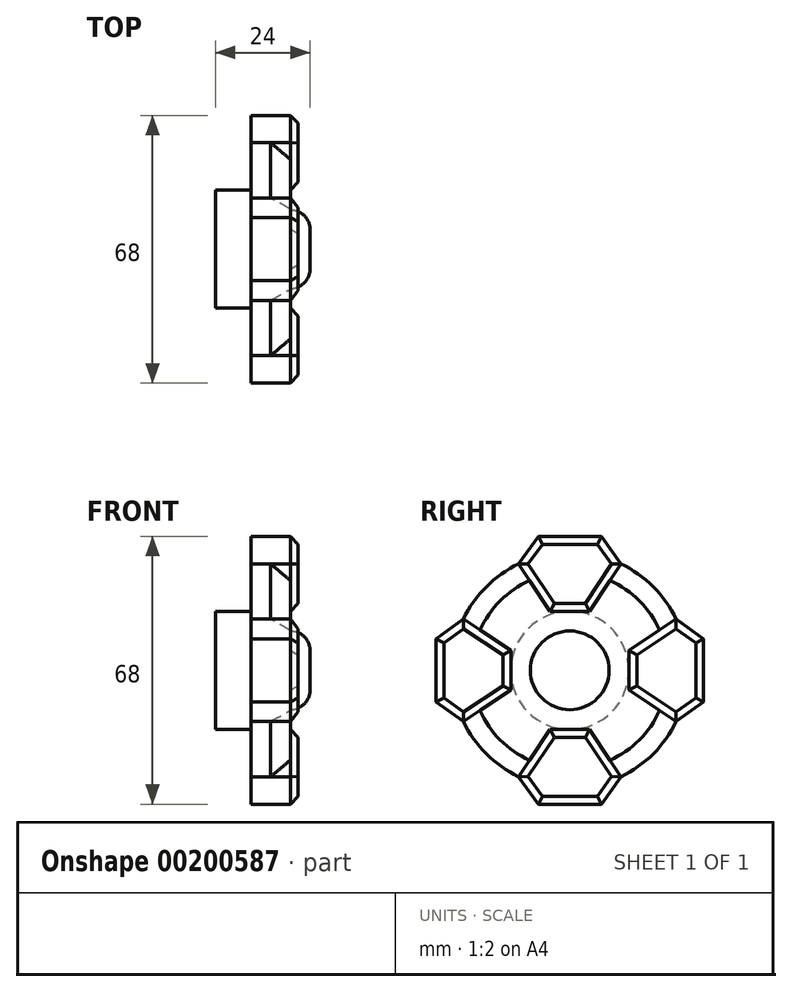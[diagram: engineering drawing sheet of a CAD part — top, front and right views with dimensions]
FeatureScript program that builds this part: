
annotation { "Feature Type Name" : "Feature", "Feature Type Description" : "" }
export const myFeature = defineFeature(function(context is Context, id is Id, definition is map)
    precondition{}
    {
        {
            var Q0;
            Q0=qCreatedBy(makeId("Right.planeOp"),FACE);
            var sketch = newSketch(context, id + "F0", { "sketchPlane" : qUnion([Q0])});
            skCircle(sketch, "E0", {"center": v(0, 0) * mm, "radius": 30 * mm});
            skLineSegment(sketch, "E1", {"start": v(0, 0) * mm, "end": v(0, 30) * mm, "construction": true});
            skLineSegment(sketch, "E2", {"start": v(0, 34) * mm, "end": v(-8, 34) * mm});
            skLineSegment(sketch, "E3", {"start": v(-8, 34) * mm, "end": v(-13, 27.04) * mm});
            skLineSegment(sketch, "E4", {"start": v(-13, 27.04) * mm, "end": v(-5, 15) * mm});
            skLineSegment(sketch, "E5", {"start": v(-5, 15) * mm, "end": v(0, 15) * mm});
            skLineSegment(sketch, "E6.MirrorCS", {"start": v(0, 34) * mm, "end": v(8, 34) * mm});
            skLineSegment(sketch, "E7.MirrorCS", {"start": v(8, 34) * mm, "end": v(13, 27.04) * mm});
            skLineSegment(sketch, "E8.MirrorCS", {"start": v(13, 27.04) * mm, "end": v(5, 15) * mm});
            skLineSegment(sketch, "E9.MirrorCS", {"start": v(5, 15) * mm, "end": v(0, 15) * mm});
            skLineSegment(sketch, "E10.1.0", {"start": v(-34, 8) * mm, "end": v(-27.04, 13) * mm});
            skLineSegment(sketch, "E10.1.1", {"start": v(-34, 0) * mm, "end": v(-34, 8) * mm});
            skLineSegment(sketch, "E10.1.2", {"start": v(-34, 0) * mm, "end": v(-34, -8) * mm});
            skLineSegment(sketch, "E10.1.3", {"start": v(-34, -8) * mm, "end": v(-27.04, -13) * mm});
            skLineSegment(sketch, "E10.1.4", {"start": v(-27.04, -13) * mm, "end": v(-15, -5) * mm});
            skLineSegment(sketch, "E10.1.5", {"start": v(-27.04, 13) * mm, "end": v(-15, 5) * mm});
            skLineSegment(sketch, "E10.1.6", {"start": v(-15, 5) * mm, "end": v(-15, 0) * mm});
            skLineSegment(sketch, "E10.1.7", {"start": v(-15, -5) * mm, "end": v(-15, 0) * mm});
            skLineSegment(sketch, "E10.2.0", {"start": v(-8, -34) * mm, "end": v(-13, -27.04) * mm});
            skLineSegment(sketch, "E10.2.1", {"start": v(0, -34) * mm, "end": v(-8, -34) * mm});
            skLineSegment(sketch, "E10.2.2", {"start": v(0, -34) * mm, "end": v(8, -34) * mm});
            skLineSegment(sketch, "E10.2.3", {"start": v(8, -34) * mm, "end": v(13, -27.04) * mm});
            skLineSegment(sketch, "E10.2.4", {"start": v(13, -27.04) * mm, "end": v(5, -15) * mm});
            skLineSegment(sketch, "E10.2.5", {"start": v(-13, -27.04) * mm, "end": v(-5, -15) * mm});
            skLineSegment(sketch, "E10.2.6", {"start": v(-5, -15) * mm, "end": v(0, -15) * mm});
            skLineSegment(sketch, "E10.2.7", {"start": v(5, -15) * mm, "end": v(0, -15) * mm});
            skLineSegment(sketch, "E10.3.0", {"start": v(34, -8) * mm, "end": v(27.04, -13) * mm});
            skLineSegment(sketch, "E10.3.1", {"start": v(34, 0) * mm, "end": v(34, -8) * mm});
            skLineSegment(sketch, "E10.3.2", {"start": v(34, 0) * mm, "end": v(34, 8) * mm});
            skLineSegment(sketch, "E10.3.3", {"start": v(34, 8) * mm, "end": v(27.04, 13) * mm});
            skLineSegment(sketch, "E10.3.4", {"start": v(27.04, 13) * mm, "end": v(15, 5) * mm});
            skLineSegment(sketch, "E10.3.5", {"start": v(27.04, -13) * mm, "end": v(15, -5) * mm});
            skLineSegment(sketch, "E10.3.6", {"start": v(15, -5) * mm, "end": v(15, 0) * mm});
            skLineSegment(sketch, "E10.3.7", {"start": v(15, 5) * mm, "end": v(15, 0) * mm});
            skSolve(sketch);
        }
        {
            var Q0;
            {var subQ2=sQuery(id+"F0.wireOp",EDGE,"E4");Q0=makeQuery(id+"F0.imprint","IMPRINT",FACE,{"disambiguationData":[TD([[makeQuery(id+"F0.imprint","IMPRINT",EDGE,{"derivedFrom":subQ2}),-1.0]])]});}
            extrude(context, id + "F1", {"entities" : qUnion([Q0]), "depth" : 10 * mm});
        }
        {
            var Q0;
            {var subQ1=sQuery(id+"F0.wireOp",EDGE,"E10.3.4");Q0=makeQuery(id+"F0.imprint","IMPRINT",FACE,{"disambiguationData":[TD([[makeQuery(id+"F0.imprint","IMPRINT",EDGE,{"derivedFrom":subQ1}),1.0]])]});}
            var Q1;
            {var subQ0=sQuery(id+"F0.wireOp",EDGE,"E10.3.0");Q1=makeQuery(id+"F0.imprint","IMPRINT",FACE,{"disambiguationData":[TD([[makeQuery(id+"F0.imprint","IMPRINT",EDGE,{"derivedFrom":subQ0}),-1.0]])]});}
            var Q2;
            {var subQ1=sQuery(id+"F0.wireOp",EDGE,"E4");Q2=makeQuery(id+"F0.imprint","IMPRINT",FACE,{"disambiguationData":[TD([[makeQuery(id+"F0.imprint","IMPRINT",EDGE,{"derivedFrom":subQ1}),1.0]])]});}
            var Q3;
            Q3=makeQuery(id+"F0.imprint","IMPRINT",FACE,{"disambiguationData":[TD([[makeQuery(id+"F0.imprint","IMPRINT",EDGE,{"derivedFrom":sQuery(id+"F0.wireOp",EDGE,"E2")}),1.0]])]});
            var Q4;
            {var subQ1=sQuery(id+"F0.wireOp",EDGE,"E10.1.4");Q4=makeQuery(id+"F0.imprint","IMPRINT",FACE,{"disambiguationData":[TD([[makeQuery(id+"F0.imprint","IMPRINT",EDGE,{"derivedFrom":subQ1}),1.0]])]});}
            var Q5;
            {var subQ0=sQuery(id+"F0.wireOp",EDGE,"E10.1.0");Q5=makeQuery(id+"F0.imprint","IMPRINT",FACE,{"disambiguationData":[TD([[makeQuery(id+"F0.imprint","IMPRINT",EDGE,{"derivedFrom":subQ0}),-1.0]])]});}
            var Q6;
            {var subQ1=sQuery(id+"F0.wireOp",EDGE,"E10.2.4");Q6=makeQuery(id+"F0.imprint","IMPRINT",FACE,{"disambiguationData":[TD([[makeQuery(id+"F0.imprint","IMPRINT",EDGE,{"derivedFrom":subQ1}),1.0]])]});}
            var Q7;
            {var subQ0=sQuery(id+"F0.wireOp",EDGE,"E10.2.0");Q7=makeQuery(id+"F0.imprint","IMPRINT",FACE,{"disambiguationData":[TD([[makeQuery(id+"F0.imprint","IMPRINT",EDGE,{"derivedFrom":subQ0}),-1.0]])]});}
            extrude(context, id + "F2", {"entities" : qUnion([Q0, Q1, Q2, Q3, Q4, Q5, Q6, Q7]), "operationType" : NewBodyOperationType.ADD, "depth" : 12 * mm});
        }
        {
            var Q0;
            {var subQ0=sQuery(id+"F0.wireOp",EDGE,"E0");Q0=makeQuery(id+"F1.opExtrude","CAP_EDGE",EDGE,{"disambiguationData":[OSD([subQ0]),TDD([makeQuery(id+"F0.imprint","IMPRINT",EDGE,{"disambiguationData":[TD([[makeQuery(id+"F0.imprint","INTERSECT",VERTEX,{"derivedFrom":[subQ0,sQuery(id+"F0.wireOp",EDGE,"E7.MirrorCS"),sQuery(id+"F0.wireOp",EDGE,"E8.MirrorCS")]}),1.0]])],"derivedFrom":subQ0})])],"isStart":false});}
            var Q1;
            {var subQ0=sQuery(id+"F0.wireOp",EDGE,"E0");Q1=makeQuery(id+"F1.opExtrude","CAP_EDGE",EDGE,{"disambiguationData":[OSD([subQ0]),TDD([makeQuery(id+"F0.imprint","IMPRINT",EDGE,{"disambiguationData":[TD([[makeQuery(id+"F0.imprint","INTERSECT",VERTEX,{"derivedFrom":[subQ0,sQuery(id+"F0.wireOp",EDGE,"E3"),sQuery(id+"F0.wireOp",EDGE,"E4")]}),-1.0]])],"derivedFrom":subQ0})])],"isStart":false});}
            var Q2;
            {var subQ0=sQuery(id+"F0.wireOp",EDGE,"E0");Q2=makeQuery(id+"F1.opExtrude","CAP_EDGE",EDGE,{"disambiguationData":[OSD([subQ0]),TDD([makeQuery(id+"F0.imprint","IMPRINT",EDGE,{"disambiguationData":[TD([[makeQuery(id+"F0.imprint","INTERSECT",VERTEX,{"derivedFrom":[subQ0,sQuery(id+"F0.wireOp",EDGE,"E10.1.3"),sQuery(id+"F0.wireOp",EDGE,"E10.1.4")]}),-1.0]])],"derivedFrom":subQ0})])],"isStart":false});}
            var Q3;
            {var subQ0=sQuery(id+"F0.wireOp",EDGE,"E0");Q3=makeQuery(id+"F1.opExtrude","CAP_EDGE",EDGE,{"disambiguationData":[OSD([subQ0]),TDD([makeQuery(id+"F0.imprint","IMPRINT",EDGE,{"disambiguationData":[TD([[makeQuery(id+"F0.imprint","INTERSECT",VERTEX,{"derivedFrom":[subQ0,sQuery(id+"F0.wireOp",EDGE,"E10.2.3"),sQuery(id+"F0.wireOp",EDGE,"E10.2.4")]}),-1.0]])],"derivedFrom":subQ0})])],"isStart":false});}
            chamfer(context, id + "F3", {"entities" : qUnion([Q0, Q1, Q2, Q3]), "width" : 5 * mm, "tangentPropagation" : true});
        }
        {
            var Q0;
            Q0=makeQuery(id+"F2.opExtrude","CAP_EDGE",EDGE,{"disambiguationData":[OSD([sQuery(id+"F0.wireOp",EDGE,"E2"),sQuery(id+"F0.wireOp",EDGE,"E6.MirrorCS")])],"isStart":false});
            var Q1;
            Q1=makeQuery(id+"F2.opExtrude","CAP_EDGE",EDGE,{"disambiguationData":[OSD([sQuery(id+"F0.wireOp",EDGE,"E3")])],"isStart":false});
            var Q2;
            Q2=makeQuery(id+"F2.opExtrude","CAP_EDGE",EDGE,{"disambiguationData":[OSD([sQuery(id+"F0.wireOp",EDGE,"E7.MirrorCS")])],"isStart":false});
            var Q3;
            Q3=makeQuery(id+"F2.opExtrude","CAP_EDGE",EDGE,{"disambiguationData":[OSD([sQuery(id+"F0.wireOp",EDGE,"E4")])],"isStart":false});
            var Q4;
            Q4=makeQuery(id+"F2.opExtrude","CAP_EDGE",EDGE,{"disambiguationData":[OSD([sQuery(id+"F0.wireOp",EDGE,"E8.MirrorCS")])],"isStart":false});
            var Q5;
            Q5=makeQuery(id+"F2.opExtrude","CAP_EDGE",EDGE,{"disambiguationData":[OSD([sQuery(id+"F0.wireOp",EDGE,"E5"),sQuery(id+"F0.wireOp",EDGE,"E9.MirrorCS")])],"isStart":false});
            var Q6;
            Q6=makeQuery(id+"F2.opExtrude","CAP_EDGE",EDGE,{"disambiguationData":[OSD([sQuery(id+"F0.wireOp",EDGE,"E10.1.6"),sQuery(id+"F0.wireOp",EDGE,"E10.1.7")])],"isStart":false});
            var Q7;
            Q7=makeQuery(id+"F2.opExtrude","CAP_EDGE",EDGE,{"disambiguationData":[OSD([sQuery(id+"F0.wireOp",EDGE,"E10.1.5")])],"isStart":false});
            var Q8;
            Q8=makeQuery(id+"F2.opExtrude","CAP_EDGE",EDGE,{"disambiguationData":[OSD([sQuery(id+"F0.wireOp",EDGE,"E10.1.0")])],"isStart":false});
            var Q9;
            Q9=makeQuery(id+"F2.opExtrude","CAP_EDGE",EDGE,{"disambiguationData":[OSD([sQuery(id+"F0.wireOp",EDGE,"E10.1.1"),sQuery(id+"F0.wireOp",EDGE,"E10.1.2")])],"isStart":false});
            var Q10;
            Q10=makeQuery(id+"F2.opExtrude","CAP_EDGE",EDGE,{"disambiguationData":[OSD([sQuery(id+"F0.wireOp",EDGE,"E10.1.3")])],"isStart":false});
            var Q11;
            Q11=makeQuery(id+"F2.opExtrude","CAP_EDGE",EDGE,{"disambiguationData":[OSD([sQuery(id+"F0.wireOp",EDGE,"E10.1.4")])],"isStart":false});
            var Q12;
            Q12=makeQuery(id+"F2.opExtrude","CAP_EDGE",EDGE,{"disambiguationData":[OSD([sQuery(id+"F0.wireOp",EDGE,"E10.2.6"),sQuery(id+"F0.wireOp",EDGE,"E10.2.7")])],"isStart":false});
            var Q13;
            Q13=makeQuery(id+"F2.opExtrude","CAP_EDGE",EDGE,{"disambiguationData":[OSD([sQuery(id+"F0.wireOp",EDGE,"E10.2.5")])],"isStart":false});
            var Q14;
            Q14=makeQuery(id+"F2.opExtrude","CAP_EDGE",EDGE,{"disambiguationData":[OSD([sQuery(id+"F0.wireOp",EDGE,"E10.2.0")])],"isStart":false});
            var Q15;
            Q15=makeQuery(id+"F2.opExtrude","CAP_EDGE",EDGE,{"disambiguationData":[OSD([sQuery(id+"F0.wireOp",EDGE,"E10.2.1"),sQuery(id+"F0.wireOp",EDGE,"E10.2.2")])],"isStart":false});
            var Q16;
            Q16=makeQuery(id+"F2.opExtrude","CAP_EDGE",EDGE,{"disambiguationData":[OSD([sQuery(id+"F0.wireOp",EDGE,"E10.2.3")])],"isStart":false});
            var Q17;
            Q17=makeQuery(id+"F2.opExtrude","CAP_EDGE",EDGE,{"disambiguationData":[OSD([sQuery(id+"F0.wireOp",EDGE,"E10.2.4")])],"isStart":false});
            var Q18;
            Q18=makeQuery(id+"F2.opExtrude","CAP_EDGE",EDGE,{"disambiguationData":[OSD([sQuery(id+"F0.wireOp",EDGE,"E10.3.6"),sQuery(id+"F0.wireOp",EDGE,"E10.3.7")])],"isStart":false});
            var Q19;
            Q19=makeQuery(id+"F2.opExtrude","CAP_EDGE",EDGE,{"disambiguationData":[OSD([sQuery(id+"F0.wireOp",EDGE,"E10.3.4")])],"isStart":false});
            var Q20;
            Q20=makeQuery(id+"F2.opExtrude","CAP_EDGE",EDGE,{"disambiguationData":[OSD([sQuery(id+"F0.wireOp",EDGE,"E10.3.3")])],"isStart":false});
            var Q21;
            Q21=makeQuery(id+"F2.opExtrude","CAP_EDGE",EDGE,{"disambiguationData":[OSD([sQuery(id+"F0.wireOp",EDGE,"E10.3.1"),sQuery(id+"F0.wireOp",EDGE,"E10.3.2")])],"isStart":false});
            var Q22;
            Q22=makeQuery(id+"F2.opExtrude","CAP_EDGE",EDGE,{"disambiguationData":[OSD([sQuery(id+"F0.wireOp",EDGE,"E10.3.5")])],"isStart":false});
            var Q23;
            Q23=makeQuery(id+"F2.opExtrude","CAP_EDGE",EDGE,{"disambiguationData":[OSD([sQuery(id+"F0.wireOp",EDGE,"E10.3.0")])],"isStart":false});
            chamfer(context, id + "F4", {"entities" : qUnion([Q0, Q1, Q2, Q3, Q4, Q5, Q6, Q7, Q8, Q9, Q10, Q11, Q12, Q13, Q14, Q15, Q16, Q17, Q18, Q19, Q20, Q21, Q22, Q23]), "width" : 2 * mm, "tangentPropagation" : true});
        }
        {
            var Q0;
            Q0=makeQuery(id+"F1.opExtrude","CAP_FACE",FACE,{"disambiguationData":[OSD([sQuery(id+"F0.wireOp",EDGE,"E0"),sQuery(id+"F0.wireOp",EDGE,"E4"),sQuery(id+"F0.wireOp",EDGE,"E5"),sQuery(id+"F0.wireOp",EDGE,"E8.MirrorCS"),sQuery(id+"F0.wireOp",EDGE,"E9.MirrorCS"),sQuery(id+"F0.wireOp",EDGE,"E10.1.4"),sQuery(id+"F0.wireOp",EDGE,"E10.1.5"),sQuery(id+"F0.wireOp",EDGE,"E10.1.6"),sQuery(id+"F0.wireOp",EDGE,"E10.1.7"),sQuery(id+"F0.wireOp",EDGE,"E10.2.4"),sQuery(id+"F0.wireOp",EDGE,"E10.2.5"),sQuery(id+"F0.wireOp",EDGE,"E10.2.6"),sQuery(id+"F0.wireOp",EDGE,"E10.2.7"),sQuery(id+"F0.wireOp",EDGE,"E10.3.4"),sQuery(id+"F0.wireOp",EDGE,"E10.3.5"),sQuery(id+"F0.wireOp",EDGE,"E10.3.6"),sQuery(id+"F0.wireOp",EDGE,"E10.3.7")])],"isStart":false});
            var sketch = newSketch(context, id + "F5", { "sketchPlane" : qUnion([Q0])});
            skCircle(sketch, "E11", {"center": v(0, 0) * mm, "radius": 10 * mm});
            skSolve(sketch);
        }
        {
            var Q0;
            Q0=makeQuery(id+"F5.imprint","IMPRINT",FACE,{"disambiguationData":[TD([[makeQuery(id+"F5.imprint","IMPRINT",EDGE,{"derivedFrom":sQuery(id+"F5.wireOp",EDGE,"E11")}),1.0]])]});
            extrude(context, id + "F6", {"entities" : qUnion([Q0]), "depth" : 5 * mm});
        }
        {
            var Q0;
            Q0=makeQuery(id+"F6.opExtrude","CAP_EDGE",EDGE,{"disambiguationData":[OSD([sQuery(id+"F5.wireOp",EDGE,"E11")])],"isStart":false});
            fillet(context, id + "F7", {"entities" : qUnion([Q0]), "radius" : 5 * mm, "tangentPropagation" : true, "allowEdgeOverflow" : false});
        }
        {
            var Q0;
            {var subQ2=sQuery(id+"F0.wireOp",EDGE,"E4");Q0=makeQuery(id+"F0.imprint","IMPRINT",FACE,{"disambiguationData":[TD([[makeQuery(id+"F0.imprint","IMPRINT",EDGE,{"derivedFrom":subQ2}),-1.0]])]});}
            var sketch = newSketch(context, id + "F8", { "sketchPlane" : qUnion([Q0])});
            skCircle(sketch, "E12", {"center": v(0, 0) * mm, "radius": 15 * mm});
            skSolve(sketch);
        }
        {
            var Q0;
            {var subQ0=sQuery(id+"F8.wireOp",EDGE,"E12");var subQ1=makeQuery(id+"F8.imprint","INTERSECT",VERTEX,{"derivedFrom":[makeQuery(id+"F0.imprint","IMPRINT",EDGE,{"derivedFrom":sQuery(id+"F0.wireOp",EDGE,"E5")}),makeQuery(id+"F0.imprint","IMPRINT",EDGE,{"derivedFrom":sQuery(id+"F0.wireOp",EDGE,"E9.MirrorCS")}),subQ0]});Q0=makeQuery(id+"F8.imprint","IMPRINT",FACE,{"disambiguationData":[TD([[makeQuery(id+"F8.imprint","IMPRINT",EDGE,{"disambiguationData":[TD([[subQ1,1.0]])],"derivedFrom":subQ0}),1.0]])]});}
            extrude(context, id + "F9", {"entities" : qUnion([Q0]), "operationType" : NewBodyOperationType.ADD, "oppositeDirection" : true, "depth" : 9 * mm});
        }
    });
